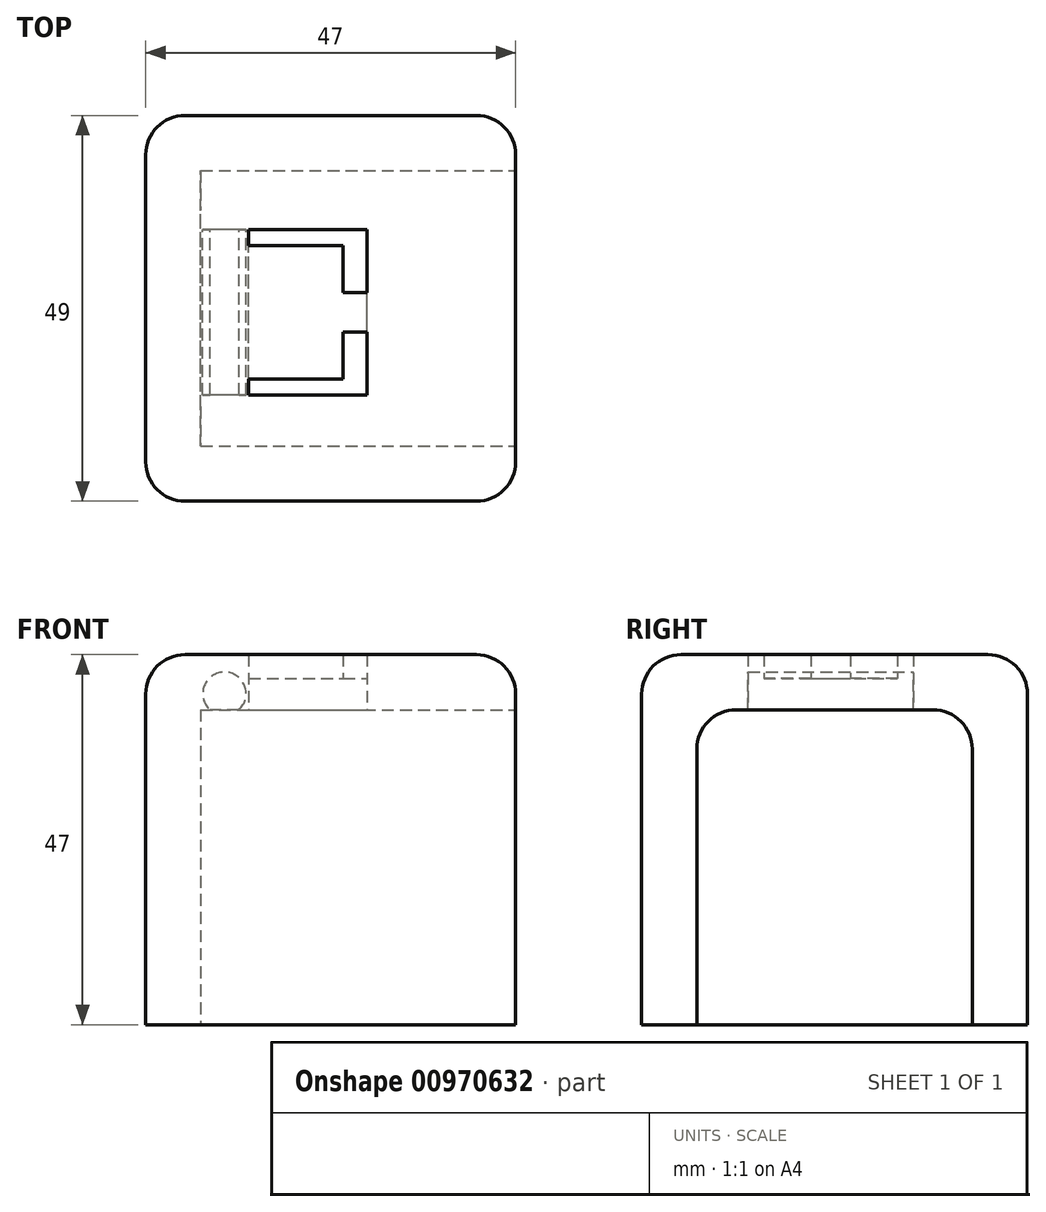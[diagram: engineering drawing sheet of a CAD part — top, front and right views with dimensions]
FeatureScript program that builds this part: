
annotation { "Feature Type Name" : "Feature", "Feature Type Description" : "" }
export const myFeature = defineFeature(function(context is Context, id is Id, definition is map)
    precondition{}
    {
        {
            var Q0;
            Q0=qCreatedBy(makeId("Front.planeOp"),FACE);
            var sketch = newSketch(context, id + "F0", { "sketchPlane" : qUnion([Q0])});
            skLineSegment(sketch, "E0.bottom", {"start": v(-55.45, 29.53) * mm, "end": v(-8.45, 29.53) * mm});
            skLineSegment(sketch, "E0.top", {"start": v(-55.45, -17.47) * mm, "end": v(-8.45, -17.47) * mm});
            skLineSegment(sketch, "E0.left", {"start": v(-55.45, 29.53) * mm, "end": v(-55.45, -17.47) * mm});
            skLineSegment(sketch, "E0.right", {"start": v(-8.45, 29.53) * mm, "end": v(-8.45, -17.47) * mm});
            skSolve(sketch);
        }
        {
            var Q0;
            Q0=makeQuery(id+"F0.imprint","IMPRINT",FACE,{"disambiguationData":[TD([[makeQuery(id+"F0.imprint","IMPRINT",EDGE,{"derivedFrom":sQuery(id+"F0.wireOp",EDGE,"E0.bottom")}),-1.0]])]});
            extrude(context, id + "F1", {"entities" : qUnion([Q0]), "depth" : 49 * mm, "offsetDistance" : 25 * mm});
        }
        {
            var Q0;
            Q0=makeQuery(id+"F1.opExtrude","SWEPT_FACE",FACE,{"disambiguationData":[OSD([sQuery(id+"F0.wireOp",EDGE,"E0.right")])]});
            var sketch = newSketch(context, id + "F2", { "sketchPlane" : qUnion([Q0])});
            skLineSegment(sketch, "E1.bottom", {"start": v(-37, 22.53) * mm, "end": v(-12, 22.53) * mm});
            skLineSegment(sketch, "E1.top", {"start": v(-42, -17.47) * mm, "end": v(-7, -17.47) * mm});
            skLineSegment(sketch, "E1.left", {"start": v(-42, 17.53) * mm, "end": v(-42, -17.47) * mm});
            skLineSegment(sketch, "E1.right", {"start": v(-7, 17.53) * mm, "end": v(-7, -17.47) * mm});
            skPoint(sketch, "E2.visualSharp", {"position": v(-42, 22.53) * mm});
            skArc(sketch, "E2.filletArc", {"start": v(-37, 22.53) * mm, "mid": v(-40.54, 21.07) * mm, "end": v(-42, 17.53) * mm});
            skPoint(sketch, "E3.visualSharp", {"position": v(-7, 22.53) * mm});
            skArc(sketch, "E3.filletArc", {"start": v(-7, 17.53) * mm, "mid": v(-8.46, 21.07) * mm, "end": v(-12, 22.53) * mm});
            skSolve(sketch);
        }
        {
            var Q0;
            Q0 = qSketchRegion(id + "F2", true);
            extrude(context, id + "F3", {"entities" : qUnion([Q0]), "operationType" : NewBodyOperationType.REMOVE, "oppositeDirection" : true, "depth" : 40 * mm, "offsetDistance" : 25 * mm});
        }
        {
            var Q0;
            Q0=makeQuery(id+"F1.opExtrude","CAP_EDGE",EDGE,{"disambiguationData":[OSD([sQuery(id+"F0.wireOp",EDGE,"E0.bottom")])],"isStart":false});
            var Q1;
            Q1=makeQuery(id+"F1.opExtrude","CAP_EDGE",EDGE,{"disambiguationData":[OSD([sQuery(id+"F0.wireOp",EDGE,"E0.right")])],"isStart":false});
            var Q2;
            Q2=makeQuery(id+"F1.opExtrude","SWEPT_EDGE",EDGE,{"disambiguationData":[OSD([sQuery(id+"F0.wireOp",EDGE,"E0.bottom"),sQuery(id+"F0.wireOp",EDGE,"E0.right")])]});
            var Q3;
            Q3=makeQuery(id+"F1.opExtrude","CAP_EDGE",EDGE,{"disambiguationData":[OSD([sQuery(id+"F0.wireOp",EDGE,"E0.right")])],"isStart":true});
            var Q4;
            Q4=makeQuery(id+"F1.opExtrude","CAP_EDGE",EDGE,{"disambiguationData":[OSD([sQuery(id+"F0.wireOp",EDGE,"E0.bottom")])],"isStart":true});
            var Q5;
            Q5=makeQuery(id+"F1.opExtrude","SWEPT_EDGE",EDGE,{"disambiguationData":[OSD([sQuery(id+"F0.wireOp",EDGE,"E0.bottom"),sQuery(id+"F0.wireOp",EDGE,"E0.left")])]});
            var Q6;
            Q6=makeQuery(id+"F1.opExtrude","CAP_EDGE",EDGE,{"disambiguationData":[OSD([sQuery(id+"F0.wireOp",EDGE,"E0.left")])],"isStart":true});
            var Q7;
            Q7=makeQuery(id+"F1.opExtrude","CAP_EDGE",EDGE,{"disambiguationData":[OSD([sQuery(id+"F0.wireOp",EDGE,"E0.left")])],"isStart":false});
            var Q8;
            Q8=makeQuery(id+"F3.boolean.opBoolean","COPY",EDGE,{"derivedFrom":makeQuery(id+"F3.opExtrude","CAP_EDGE",EDGE,{"disambiguationData":[OSD([sQuery(id+"F2.wireOp",EDGE,"E1.bottom")])],"isStart":true})});
            fillet(context, id + "F4", {"entities" : qUnion([Q0, Q1, Q2, Q3, Q4, Q5, Q6, Q7, Q8]), "radius" : 5 * mm, "tangentPropagation" : true, "allowEdgeOverflow" : false});
        }
        {
            var Q0;
            Q0=qCreatedBy(makeId("Front.planeOp"),FACE);
            cPlane(context, id + "F5", {"entities" : qUnion([Q0]), "cplaneType" : CPlaneType.OFFSET, "offset" : 14.5 * mm, "width" : 150 * mm, "height" : 150 * mm});
        }
        {
            var Q0;
            Q0=qCreatedBy(id+"F5.planeOp",FACE);
            var sketch = newSketch(context, id + "F6", { "sketchPlane" : qUnion([Q0])});
            skCircle(sketch, "E4", {"center": v(-45.45, 24.57) * mm, "radius": 2.75 * mm});
            skSolve(sketch);
        }
        {
            var Q0;
            Q0=makeQuery(id+"F6.imprint","IMPRINT",FACE,{"disambiguationData":[TD([[makeQuery(id+"F6.imprint","IMPRINT",EDGE,{"derivedFrom":sQuery(id+"F6.wireOp",EDGE,"E4")}),1.0]])]});
            extrude(context, id + "F7", {"entities" : qUnion([Q0]), "operationType" : NewBodyOperationType.REMOVE, "depth" : 21 * mm, "offsetDistance" : 25 * mm});
        }
        {
            var Q0;
            Q0=makeQuery(id+"F3.boolean.opBoolean","COPY",FACE,{"derivedFrom":makeQuery(id+"F3.opExtrude","SWEPT_FACE",FACE,{"disambiguationData":[OSD([sQuery(id+"F2.wireOp",EDGE,"E1.bottom")])]})});
            var sketch = newSketch(context, id + "F8", { "sketchPlane" : qUnion([Q0])});
            skLineSegment(sketch, "E5.bottom", {"start": v(-42.36, 35.5) * mm, "end": v(-27.36, 35.5) * mm});
            skLineSegment(sketch, "E5.top", {"start": v(-42.36, 14.5) * mm, "end": v(-27.36, 14.5) * mm});
            skLineSegment(sketch, "E5.left", {"start": v(-42.36, 35.5) * mm, "end": v(-42.36, 14.5) * mm});
            skLineSegment(sketch, "E5.right", {"start": v(-27.36, 35.5) * mm, "end": v(-27.36, 14.5) * mm});
            skSolve(sketch);
        }
        {
            var Q0;
            Q0=makeQuery(id+"F8.imprint","IMPRINT",FACE,{"disambiguationData":[TD([[makeQuery(id+"F8.imprint","IMPRINT",EDGE,{"derivedFrom":sQuery(id+"F8.wireOp",EDGE,"E5.bottom")}),-1.0]])]});
            extrude(context, id + "F9", {"entities" : qUnion([Q0]), "operationType" : NewBodyOperationType.REMOVE, "oppositeDirection" : true, "depth" : 4 * mm, "offsetDistance" : 25 * mm});
        }
        {
            var Q0;
            Q0=makeQuery(id+"F9.boolean.opBoolean","COPY",FACE,{"derivedFrom":makeQuery(id+"F9.opExtrude","CAP_FACE",FACE,{"disambiguationData":[OSD([sQuery(id+"F8.wireOp",EDGE,"E5.bottom"),sQuery(id+"F8.wireOp",EDGE,"E5.top"),sQuery(id+"F8.wireOp",EDGE,"E5.left"),sQuery(id+"F8.wireOp",EDGE,"E5.right")])],"isStart":false})});
            var sketch = newSketch(context, id + "F10", { "sketchPlane" : qUnion([Q0])});
            skLineSegment(sketch, "E6.bottom", {"start": v(-42.36, 35.5) * mm, "end": v(-27.36, 35.5) * mm});
            skLineSegment(sketch, "E6.top", {"start": v(-42.36, 33.5) * mm, "end": v(-27.36, 33.5) * mm});
            skLineSegment(sketch, "E6.left", {"start": v(-42.36, 35.5) * mm, "end": v(-42.36, 33.5) * mm});
            skLineSegment(sketch, "E6.right", {"start": v(-27.36, 35.5) * mm, "end": v(-27.36, 33.5) * mm});
            skLineSegment(sketch, "E7.bottom", {"start": v(-42.36, 16.5) * mm, "end": v(-30.36, 16.5) * mm});
            skLineSegment(sketch, "E7.top", {"start": v(-42.36, 14.5) * mm, "end": v(-30.36, 14.5) * mm});
            skLineSegment(sketch, "E7.left", {"start": v(-42.36, 16.5) * mm, "end": v(-42.36, 14.5) * mm});
            skLineSegment(sketch, "E7.right", {"start": v(-30.36, 16.5) * mm, "end": v(-30.36, 14.5) * mm});
            skLineSegment(sketch, "E8.bottom", {"start": v(-30.36, 14.5) * mm, "end": v(-27.36, 14.5) * mm});
            skLineSegment(sketch, "E8.top", {"start": v(-30.36, 35.5) * mm, "end": v(-27.36, 35.5) * mm});
            skLineSegment(sketch, "E8.left", {"start": v(-30.36, 14.5) * mm, "end": v(-30.36, 35.5) * mm});
            skLineSegment(sketch, "E8.right", {"start": v(-27.36, 14.5) * mm, "end": v(-27.36, 35.5) * mm});
            skLineSegment(sketch, "E9.bottom", {"start": v(-30.36, 27.5) * mm, "end": v(-27.36, 27.5) * mm});
            skLineSegment(sketch, "E9.top", {"start": v(-30.36, 22.5) * mm, "end": v(-27.36, 22.5) * mm});
            skLineSegment(sketch, "E9.left", {"start": v(-30.36, 27.5) * mm, "end": v(-30.36, 22.5) * mm});
            skLineSegment(sketch, "E9.right", {"start": v(-27.36, 27.5) * mm, "end": v(-27.36, 22.5) * mm});
            skSolve(sketch);
        }
        {
            var Q0;
            {var subQ5=sQuery(id+"F10.wireOp",EDGE,"E9.bottom");Q0=makeQuery(id+"F10.imprint","IMPRINT",FACE,{"disambiguationData":[TD([[makeQuery(id+"F10.imprint","IMPRINT",EDGE,{"derivedFrom":subQ5}),1.0]])]});}
            var Q1;
            {var subQ1=sQuery(id+"F10.wireOp",EDGE,"E8.bottom");Q1=makeQuery(id+"F10.imprint","IMPRINT",FACE,{"disambiguationData":[TD([[makeQuery(id+"F10.imprint","IMPRINT",EDGE,{"derivedFrom":subQ1}),1.0]])]});}
            var Q2;
            {var subQ0=sQuery(id+"F10.wireOp",EDGE,"E6.bottom");Q2=makeQuery(id+"F10.imprint","IMPRINT",FACE,{"disambiguationData":[TD([[makeQuery(id+"F10.imprint","IMPRINT",EDGE,{"derivedFrom":subQ0}),-1.0]])]});}
            var Q3;
            {var subQ5=sQuery(id+"F10.wireOp",EDGE,"E8.top");Q3=makeQuery(id+"F10.imprint","IMPRINT",FACE,{"disambiguationData":[TD([[makeQuery(id+"F10.imprint","IMPRINT",EDGE,{"derivedFrom":subQ5}),-1.0]])]});}
            var Q4;
            {var subQ0=sQuery(id+"F10.wireOp",EDGE,"E7.bottom");Q4=makeQuery(id+"F10.imprint","IMPRINT",FACE,{"disambiguationData":[TD([[makeQuery(id+"F10.imprint","IMPRINT",EDGE,{"derivedFrom":subQ0}),-1.0]])]});}
            extrude(context, id + "F11", {"entities" : qUnion([Q0, Q1, Q2, Q3, Q4]), "operationType" : NewBodyOperationType.REMOVE, "endBound" : BoundingType.THROUGH_ALL, "oppositeDirection" : true, "depth" : 25 * mm, "offsetDistance" : 25 * mm});
        }
    });
